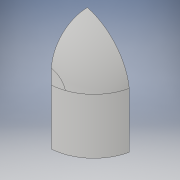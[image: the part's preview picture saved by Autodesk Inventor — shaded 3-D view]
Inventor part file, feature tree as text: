
AUTODESK INVENTOR PART (.ipt)
format: ipt  version: 2019 (Build 230136000, 136)  size: 345,088 bytes
history: native  units: mm
features: sketch x6, extrude x3, other x1, loft x1, shell x1, projected_geometry x1
ambient origin geometry x8: Origin, YZ Plane, XZ Plane, XY Plane, X Axis, Y Axis, Z Axis, Center Point
bodies: Body1 (feature_tree)
feature tree (13):
  sketch  "Эскиз3"
  sketch  "Эскиз4"
  other  "РабПлоскость1"
  loft  "Лофт1"
  extrude  "Выдавливание2"  Depth=100.0mm
  shell  "Оболочка1"  Thickness=17.0mm
  extrude  "Выдавливание3"  Depth=4.0mm
  extrude  "Выдавливание4"  Depth=35.0mm
  sketch  "Эскиз5"
  sketch  "Эскиз6"
  projected_geometry  "Спроецированная петля1"
  sketch  "Эскиз7"
  sketch  "Эскиз8"
